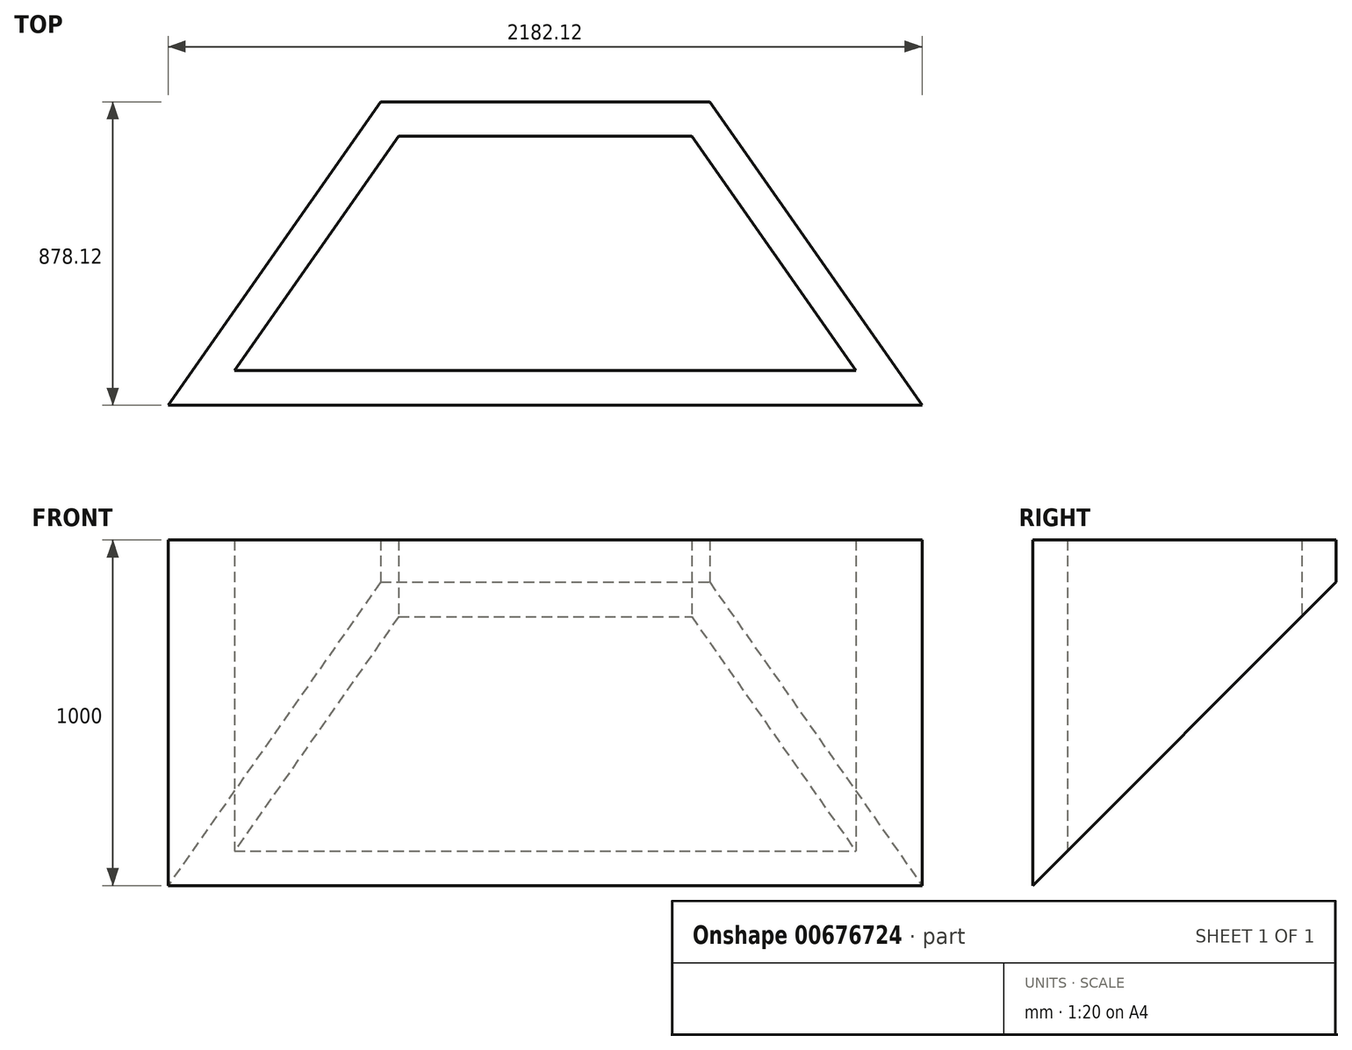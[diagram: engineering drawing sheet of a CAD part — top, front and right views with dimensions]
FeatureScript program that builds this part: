
annotation { "Feature Type Name" : "Feature", "Feature Type Description" : "" }
export const myFeature = defineFeature(function(context is Context, id is Id, definition is map)
    precondition{}
    {
        {
            var Q0;
            Q0=qCreatedBy(makeId("Top.planeOp"),FACE);
            var sketch = newSketch(context, id + "F0", { "sketchPlane" : qUnion([Q0])});
            skLineSegment(sketch, "E0", {"start": v(0, 389.06) * mm, "end": v(0, -389.06) * mm, "construction": true});
            skLineSegment(sketch, "E1", {"start": v(-450, 389.06) * mm, "end": v(-995, -389.06) * mm, "construction": true});
            skLineSegment(sketch, "E2.MirrorCS", {"start": v(450, 389.06) * mm, "end": v(995, -389.06) * mm, "construction": true});
            skLineSegment(sketch, "E3", {"start": v(-450, 389.06) * mm, "end": v(450, 389.06) * mm, "construction": true});
            skLineSegment(sketch, "E4", {"start": v(-995, -389.06) * mm, "end": v(995, -389.06) * mm, "construction": true});
            skLineSegment(sketch, "E5.0", {"start": v(-476.02, 439.06) * mm, "end": v(-1091.06, -439.06) * mm});
            skLineSegment(sketch, "E5.1", {"start": v(-476.02, 439.06) * mm, "end": v(476.02, 439.06) * mm});
            skLineSegment(sketch, "E5.2", {"start": v(476.02, 439.06) * mm, "end": v(1091.06, -439.06) * mm});
            skLineSegment(sketch, "E5.3", {"start": v(-1091.06, -439.06) * mm, "end": v(1091.06, -439.06) * mm});
            skLineSegment(sketch, "E6.0", {"start": v(-423.98, 339.06) * mm, "end": v(-898.94, -339.06) * mm});
            skLineSegment(sketch, "E6.1", {"start": v(-423.98, 339.06) * mm, "end": v(423.98, 339.06) * mm});
            skLineSegment(sketch, "E6.2", {"start": v(423.98, 339.06) * mm, "end": v(898.94, -339.06) * mm});
            skLineSegment(sketch, "E6.3", {"start": v(-898.94, -339.06) * mm, "end": v(898.94, -339.06) * mm});
            skSolve(sketch);
        }
        {
            var Q0;
            Q0=makeQuery(id+"F0.imprint","IMPRINT",FACE,{"disambiguationData":[TD([[makeQuery(id+"F0.imprint","IMPRINT",EDGE,{"derivedFrom":sQuery(id+"F0.wireOp",EDGE,"E5.0")}),1.0]])]});
            extrude(context, id + "F1", {"entities" : qUnion([Q0]), "depth" : 1000 * mm, "offsetDistance" : 25 * mm});
        }
        {
            var Q0;
            Q0=qCreatedBy(makeId("Right.planeOp"),FACE);
            var sketch = newSketch(context, id + "F2", { "sketchPlane" : qUnion([Q0])});
            skLineSegment(sketch, "E7.0", {"start": v(439.06, 0) * mm, "end": v(-439.06, 0) * mm});
            skLineSegment(sketch, "E8", {"start": v(439.06, 0) * mm, "end": v(439.06, 878.12) * mm});
            skLineSegment(sketch, "E9", {"start": v(439.06, 878.12) * mm, "end": v(-439.06, 0) * mm});
            skSolve(sketch);
        }
        {
            var Q0;
            Q0 = qSketchRegion(id + "F2", true);
            extrude(context, id + "F3", {"entities" : qUnion([Q0]), "operationType" : NewBodyOperationType.REMOVE, "endBound" : BoundingType.THROUGH_ALL, "oppositeDirection" : true, "depth" : 25 * mm, "offsetDistance" : 25 * mm, "hasSecondDirection" : true, "secondDirectionBound" : SecondDirectionBoundingType.THROUGH_ALL, "secondDirectionOppositeDirection" : false, "secondDirectionDepth" : 25 * mm});
        }
    });
